FCSTD DOCUMENT  (FreeCAD 0.20R0.20.2)
Label: 002
License: All rights reserved
LicenseURL: http://en.wikipedia.org/wiki/All_rights_reserved
objects: Sketcher::SketchObject×1
note: 1 computed .brp shape members not serialized (recipe doc carries the construction recipe); baked Part::Feature solids carry a one-line shape summary decoded from their .brp

FEATURE [Sketcher::SketchObject] Sketch
  FullyConstrained = true
  sketch-geometry (17):
    g0: LineSegment StartX=12.0586 StartY=-6 StartZ=0 EndX=12.0586 EndY=0 EndZ=0
    g1: LineSegment StartX=2.8 StartY=-6 StartZ=0 EndX=2.8 EndY=0 EndZ=0
    g2: LineSegment StartX=2.8 StartY=-6 StartZ=0 EndX=12.0586 EndY=-6 EndZ=0
    g3: LineSegment StartX=12.0586 StartY=0 StartZ=0 EndX=14 EndY=0 EndZ=0
    g4: LineSegment StartX=2.8 StartY=0 StartZ=0 EndX=0 EndY=0 EndZ=0
    g5: LineSegment StartX=14 StartY=0 StartZ=0 EndX=14 EndY=1.2 EndZ=0
    g6: LineSegment StartX=0 StartY=0 StartZ=0 EndX=0 EndY=1.2 EndZ=0
    g7: LineSegment StartX=0 StartY=0 StartZ=0 EndX=-4.6 EndY=0 EndZ=0
    g8: LineSegment StartX=-4.6 StartY=14 StartZ=0 EndX=0.2 EndY=14 EndZ=0
    g9: Circle CenterX=-2.2 CenterY=11.6 CenterZ=0 NormalX=0 NormalY=0 NormalZ=1 AngleXU=0 Radius=0.4
    g10: Circle CenterX=-2.2 CenterY=11.6 CenterZ=0 NormalX=0 NormalY=0 NormalZ=1 AngleXU=0 Radius=2.4
    g11: Circle CenterX=0 CenterY=1.2 CenterZ=0 NormalX=0 NormalY=0 NormalZ=1 AngleXU=0 Radius=1
    g12: Circle CenterX=-0.472892 CenterY=5.84375 CenterZ=0 NormalX=0 NormalY=0 NormalZ=1 AngleXU=0 Radius=1
    g13: Circle CenterX=-3.84772 CenterY=9.855 CenterZ=0 NormalX=0 NormalY=0 NormalZ=1 AngleXU=0 Radius=1
    g14: BSplineCurve PolesCount=3 KnotsCount=2 Degree=2 IsPeriodic=0
    g15: GeomPoint X=0 Y=1.2 Z=0
    g16: GeomPoint X=-3.84772 Y=9.855 Z=0
  constraints (40):
    c: Vertical(g0)
    c: Vertical(g1)
    c: Block(g1)
    c: Block(g0)
    c: Distance(g1) = 6
    c: Coincident(g2,g1)
    c: Horizontal(g2)
    c: Coincident(g0,g2)
    c: Block(g2)
    c: Coincident(g3,g0)
    c: Horizontal(g3)
    c: Coincident(g4,g1)
    c: Horizontal(g4)
    c: Block(g3)
    c: Block(g4)
    c: Coincident(g5,g3)
    c: Vertical(g5)
    c: Coincident(g6,g4)
    c: Vertical(g6)
    c: Distance(g5) = 1.2
    c: Distance(g6) = 1.2
    c: Coincident(g7,g4)
    c: Horizontal(g7)
    c: Distance(g7) = 4.6
    c: Horizontal(g8)
    c: Distance(g8) = 4.8
    c: Block(g8)
    c: Block(g9)
    c: Block(g10)
    c: PointOnObject(g14,g10)
    c: Weight(g11) = 1
    c: Coincident(g14,g6)
    c: Equal(g11,g12)
    c: Equal(g11,g13)
    c: InternalAlignment(g11,g14)
    c: InternalAlignment(g12,g14)
    c: InternalAlignment(g13,g14)
    c: InternalAlignment(g15,g14)
    c: InternalAlignment(g16,g14)
    c: Block(g14)
